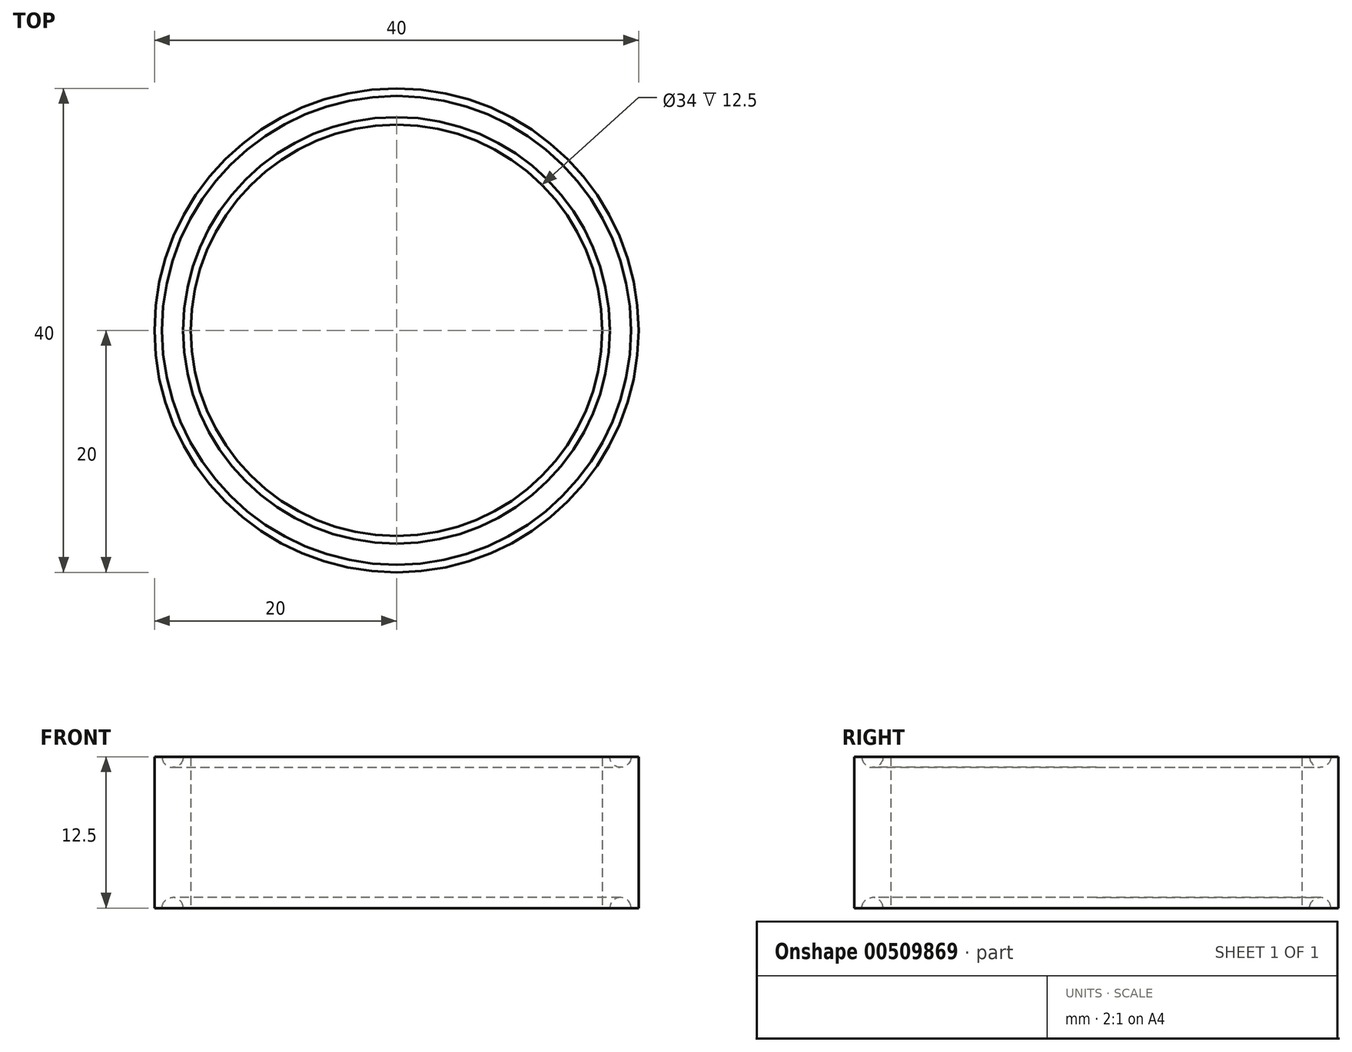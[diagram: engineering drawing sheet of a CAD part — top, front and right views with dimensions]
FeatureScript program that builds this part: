
annotation { "Feature Type Name" : "Feature", "Feature Type Description" : "" }
export const myFeature = defineFeature(function(context is Context, id is Id, definition is map)
    precondition{}
    {
        {
            var Q0;
            Q0=qCreatedBy(makeId("Top.planeOp"),FACE);
            var sketch = newSketch(context, id + "F0", { "sketchPlane" : qUnion([Q0])});
            skCircle(sketch, "E0", {"center": v(0, 0) * mm, "radius": 17 * mm});
            skCircle(sketch, "E1", {"center": v(0, 0) * mm, "radius": 20 * mm});
            skSolve(sketch);
        }
        {
            var Q0;
            Q0 = qSketchRegion(id + "F0", true);
            extrude(context, id + "F1", {"entities" : qUnion([Q0]), "depth" : ((25 / 2) / 2) * mm});
        }
        {
            var Q0;
            Q0=qCreatedBy(makeId("Front.planeOp"),FACE);
            var sketch = newSketch(context, id + "F2", { "sketchPlane" : qUnion([Q0])});
            skLineSegment(sketch, "E2", {"start": v(0, 0) * mm, "end": v(20, 0) * mm});
            skLineSegment(sketch, "E3", {"start": v(20, 0) * mm, "end": v(17, 0) * mm});
            skArc(sketch, "E4", {"start": v(19.38, 0) * mm, "mid": v(18.5, 0.87) * mm, "end": v(17.62, 0) * mm});
            skSolve(sketch);
        }
        {
            var Q0;
            Q0 = qSketchRegion(id + "F2", true);
            var Q1;
            Q1=makeQuery(id+"F1.opExtrude","CAP_EDGE",EDGE,{"disambiguationData":[OSD([sQuery(id+"F0.wireOp",EDGE,"E0")])],"isStart":true});
            revolve(context, id + "F3", {"operationType" : NewBodyOperationType.REMOVE, "entities" : qUnion([Q0]), "axis" : qUnion([Q1]), "revolveType" : RevolveType.FULL, "oppositeDirection" : true});
        }
        {
            var Q0;
            Q0=makeQuery(id+"F1.opExtrude","SWEPT_BODY",BODY,{"disambiguationData":[OSD([sQuery(id+"F0.wireOp",EDGE,"E0"),sQuery(id+"F0.wireOp",EDGE,"E1")])]});
            var Q1;
            Q1=makeQuery(id+"F1.opExtrude","CAP_FACE",FACE,{"disambiguationData":[OSD([sQuery(id+"F0.wireOp",EDGE,"E0"),sQuery(id+"F0.wireOp",EDGE,"E1")])],"isStart":false});
            mirror(context, id + "F4", {"operationType" : NewBodyOperationType.ADD, "entities" : qUnion([Q0]), "mirrorPlane" : qUnion([Q1])});
        }
    });
